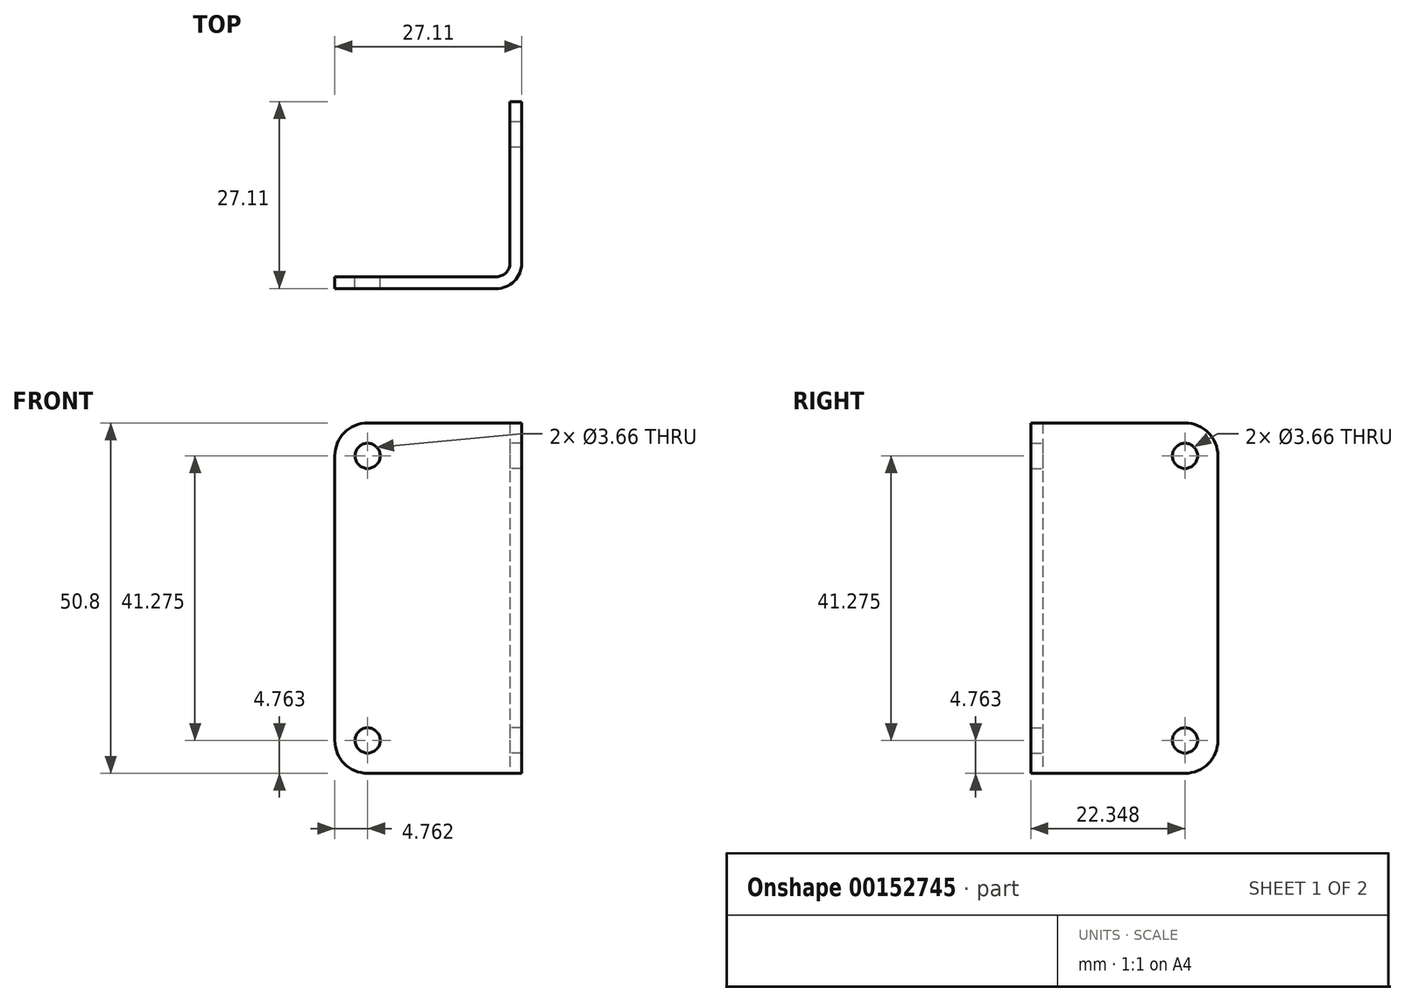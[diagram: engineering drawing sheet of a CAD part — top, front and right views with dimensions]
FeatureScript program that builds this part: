
annotation { "Feature Type Name" : "Feature", "Feature Type Description" : "" }
export const myFeature = defineFeature(function(context is Context, id is Id, definition is map)
    precondition{}
    {
        {
            var Q0;
            Q0=qCreatedBy(makeId("Top.planeOp"),FACE);
            var sketch = newSketch(context, id + "F0", { "sketchPlane" : qUnion([Q0])});
            skLineSegment(sketch, "E0.top", {"start": v(0, 25.4) * mm, "end": v(1.7, 25.4) * mm});
            skLineSegment(sketch, "E0.left", {"start": v(0, 0) * mm, "end": v(0, 25.4) * mm});
            skLineSegment(sketch, "E0.right", {"start": v(1.7, -1.7) * mm, "end": v(1.7, 25.4) * mm});
            skLineSegment(sketch, "E1.bottom", {"start": v(0, 0) * mm, "end": v(-25.4, 0) * mm});
            skLineSegment(sketch, "E1.top", {"start": v(1.7, -1.7) * mm, "end": v(-25.4, -1.7) * mm});
            skLineSegment(sketch, "E1.right", {"start": v(-25.4, 0) * mm, "end": v(-25.4, -1.7) * mm});
            skSolve(sketch);
        }
        {
            var Q0;
            Q0=qSketchRegion(id+"F0",true);
            extrude(context, id + "F1", {"entities" : qUnion([Q0]), "depth" : 50.8 * mm});
        }
        {
            var Q0;
            Q0=makeQuery(id+"F1.opExtrude","SWEPT_EDGE",EDGE,{"disambiguationData":[OSD([sQuery(id+"F0.wireOp",EDGE,"E0.left"),sQuery(id+"F0.wireOp",EDGE,"E1.bottom")])]});
            fillet(context, id + "F2", {"entities" : qUnion([Q0]), "radius" : 1.98 * mm, "tangentPropagation" : true, "allowEdgeOverflow" : false});
        }
        {
            var Q0;
            Q0=makeQuery(id+"F1.opExtrude","SWEPT_EDGE",EDGE,{"disambiguationData":[OSD([sQuery(id+"F0.wireOp",EDGE,"E0.right"),sQuery(id+"F0.wireOp",EDGE,"E1.top")])]});
            fillet(context, id + "F3", {"entities" : qUnion([Q0]), "radius" : 3.7 * mm, "tangentPropagation" : true, "allowEdgeOverflow" : false});
        }
        {
            var Q0;
            Q0=makeQuery(id+"F1.opExtrude","SWEPT_FACE",FACE,{"disambiguationData":[OSD([sQuery(id+"F0.wireOp",EDGE,"E0.left")])]});
            var sketch = newSketch(context, id + "F4", { "sketchPlane" : qUnion([Q0])});
            skLineSegment(sketch, "E2", {"start": v(-25.4, 25.4) * mm, "end": v(-20.64, 25.4) * mm, "construction": true});
            skLineSegment(sketch, "E3", {"start": v(-20.64, 46.04) * mm, "end": v(-20.64, 4.76) * mm, "construction": true});
            skLineSegment(sketch, "E4", {"start": v(-20.64, 4.76) * mm, "end": v(-20.64, 0) * mm, "construction": true});
            skCircle(sketch, "E5", {"center": v(-20.64, 46.04) * mm, "radius": 1.83 * mm});
            skCircle(sketch, "E6", {"center": v(-20.64, 4.76) * mm, "radius": 1.83 * mm});
            skSolve(sketch);
        }
        {
            var Q0;
            Q0=qSketchRegion(id+"F4",true);
            var Q1;
            Q1=makeQuery(id+"F1.opExtrude","SWEPT_FACE",FACE,{"disambiguationData":[OSD([sQuery(id+"F0.wireOp",EDGE,"E0.right")])]});
            extrude(context, id + "F5", {"entities" : qUnion([Q0]), "operationType" : NewBodyOperationType.REMOVE, "endBound" : BoundingType.UP_TO_SURFACE, "oppositeDirection" : true, "endBoundEntityFace" : qUnion([Q1]), "depth" : 25.4 * mm});
        }
        {
            var Q0;
            Q0=makeQuery(id+"F1.opExtrude","SWEPT_FACE",FACE,{"disambiguationData":[OSD([sQuery(id+"F0.wireOp",EDGE,"E1.bottom")])]});
            var sketch = newSketch(context, id + "F6", { "sketchPlane" : qUnion([Q0])});
            skLineSegment(sketch, "E7", {"start": v(25.4, 25.4) * mm, "end": v(20.64, 25.4) * mm, "construction": true});
            skLineSegment(sketch, "E8", {"start": v(20.64, 46.04) * mm, "end": v(20.64, 4.76) * mm, "construction": true});
            skLineSegment(sketch, "E9", {"start": v(20.64, 4.76) * mm, "end": v(20.64, 0) * mm, "construction": true});
            skCircle(sketch, "E10", {"center": v(20.64, 46.04) * mm, "radius": 1.83 * mm});
            skCircle(sketch, "E11", {"center": v(20.64, 4.76) * mm, "radius": 1.83 * mm});
            skSolve(sketch);
        }
        {
            var Q0;
            Q0=qSketchRegion(id+"F6",true);
            var Q1;
            Q1=makeQuery(id+"F1.opExtrude","SWEPT_FACE",FACE,{"disambiguationData":[OSD([sQuery(id+"F0.wireOp",EDGE,"E1.top")])]});
            extrude(context, id + "F7", {"entities" : qUnion([Q0]), "operationType" : NewBodyOperationType.REMOVE, "endBound" : BoundingType.UP_TO_SURFACE, "oppositeDirection" : true, "endBoundEntityFace" : qUnion([Q1]), "depth" : 25.4 * mm});
        }
        {
            var Q0;
            Q0=makeQuery(id+"F1.opExtrude","CAP_EDGE",EDGE,{"disambiguationData":[OSD([sQuery(id+"F0.wireOp",EDGE,"E0.top")])],"isStart":false});
            var Q1;
            Q1=makeQuery(id+"F1.opExtrude","CAP_EDGE",EDGE,{"disambiguationData":[OSD([sQuery(id+"F0.wireOp",EDGE,"E1.right")])],"isStart":false});
            var Q2;
            Q2=makeQuery(id+"F1.opExtrude","CAP_EDGE",EDGE,{"disambiguationData":[OSD([sQuery(id+"F0.wireOp",EDGE,"E1.right")])],"isStart":true});
            var Q3;
            Q3=makeQuery(id+"F1.opExtrude","CAP_EDGE",EDGE,{"disambiguationData":[OSD([sQuery(id+"F0.wireOp",EDGE,"E0.top")])],"isStart":true});
            fillet(context, id + "F8", {"entities" : qUnion([Q0, Q1, Q2, Q3]), "radius" : 4.76 * mm, "tangentPropagation" : true, "allowEdgeOverflow" : false});
        }
    });
